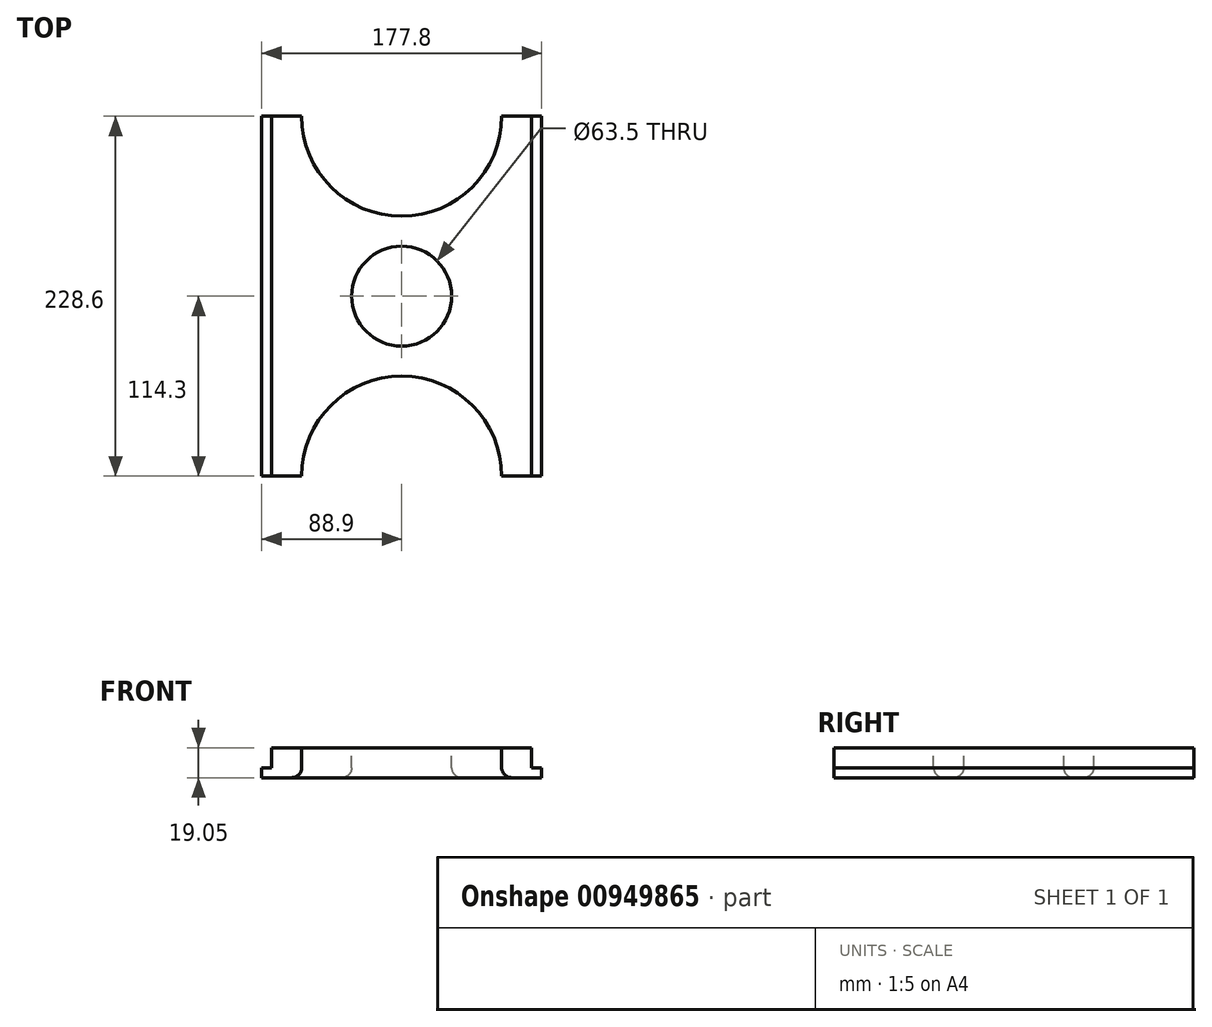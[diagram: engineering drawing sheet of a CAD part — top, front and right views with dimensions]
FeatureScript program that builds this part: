
annotation { "Feature Type Name" : "Feature", "Feature Type Description" : "" }
export const myFeature = defineFeature(function(context is Context, id is Id, definition is map)
    precondition{}
    {
        {
            var Q0;
            Q0=qCreatedBy(makeId("Top.planeOp"),FACE);
            var sketch = newSketch(context, id + "F0", { "sketchPlane" : qUnion([Q0])});
            skLineSegment(sketch, "E0.bottom", {"start": v(88.9, -114.3) * mm, "end": v(-88.9, -114.3) * mm});
            skLineSegment(sketch, "E0.top", {"start": v(88.9, 114.3) * mm, "end": v(-88.9, 114.3) * mm});
            skLineSegment(sketch, "E0.left", {"start": v(88.9, -114.3) * mm, "end": v(88.9, 114.3) * mm});
            skLineSegment(sketch, "E0.right", {"start": v(-88.9, -114.3) * mm, "end": v(-88.9, 114.3) * mm});
            skPoint(sketch, "E0.middle", {"position": v(0, 0) * mm});
            skSolve(sketch);
        }
        {
            var Q0;
            Q0 = qSketchRegion(id + "F0", true);
            extrude(context, id + "F1", {"entities" : qUnion([Q0]), "depth" : 19.05 * mm, "offsetDistance" : 25.4 * mm});
        }
        {
            var Q0;
            Q0=makeQuery(id+"F1.opExtrude","SWEPT_FACE",FACE,{"disambiguationData":[OSD([sQuery(id+"F0.wireOp",EDGE,"E0.bottom")])]});
            var sketch = newSketch(context, id + "F2", { "sketchPlane" : qUnion([Q0])});
            skLineSegment(sketch, "E1", {"start": v(82.55, 19.05) * mm, "end": v(82.55, 6.35) * mm});
            skLineSegment(sketch, "E2", {"start": v(82.55, 6.35) * mm, "end": v(88.9, 6.35) * mm});
            skLineSegment(sketch, "E3", {"start": v(88.9, 6.35) * mm, "end": v(88.9, 19.05) * mm});
            skLineSegment(sketch, "E4", {"start": v(88.9, 19.05) * mm, "end": v(82.55, 19.05) * mm});
            skLineSegment(sketch, "E5", {"start": v(-82.55, 19.05) * mm, "end": v(-82.55, 6.35) * mm});
            skLineSegment(sketch, "E6", {"start": v(-82.55, 6.35) * mm, "end": v(-88.9, 6.35) * mm});
            skLineSegment(sketch, "E7", {"start": v(-88.9, 6.35) * mm, "end": v(-88.9, 19.05) * mm});
            skLineSegment(sketch, "E8", {"start": v(-88.9, 19.05) * mm, "end": v(-82.55, 19.05) * mm});
            skSolve(sketch);
        }
        {
            var Q0;
            Q0 = qSketchRegion(id + "F2", true);
            extrude(context, id + "F3", {"entities" : qUnion([Q0]), "operationType" : NewBodyOperationType.REMOVE, "oppositeDirection" : true, "depth" : 254 * mm, "offsetDistance" : 25.4 * mm});
        }
        {
            var Q0;
            Q0=makeQuery(id+"F1.opExtrude","CAP_FACE",FACE,{"disambiguationData":[OSD([sQuery(id+"F0.wireOp",EDGE,"E0.bottom"),sQuery(id+"F0.wireOp",EDGE,"E0.top"),sQuery(id+"F0.wireOp",EDGE,"E0.left"),sQuery(id+"F0.wireOp",EDGE,"E0.right")])],"isStart":false});
            var sketch = newSketch(context, id + "F4", { "sketchPlane" : qUnion([Q0])});
            skLineSegment(sketch, "E9", {"start": v(0, 114.3) * mm, "end": v(0, -114.3) * mm, "construction": true});
            skLineSegment(sketch, "E10", {"start": v(-82.55, 0) * mm, "end": v(82.55, 0) * mm, "construction": true});
            skCircle(sketch, "E11", {"center": v(0, -114.3) * mm, "radius": 63.5 * mm});
            skCircle(sketch, "E12", {"center": v(0, 114.3) * mm, "radius": 63.5 * mm});
            skCircle(sketch, "E13", {"center": v(0, 0) * mm, "radius": 31.75 * mm});
            skSolve(sketch);
        }
        {
            var Q0;
            Q0 = qSketchRegion(id + "F4", true);
            extrude(context, id + "F5", {"entities" : qUnion([Q0]), "operationType" : NewBodyOperationType.REMOVE, "oppositeDirection" : true, "depth" : 25.4 * mm, "offsetDistance" : 25.4 * mm});
        }
        {
            var Q0;
            Q0=makeQuery(id+"F5.boolean.opBoolean","INTERSECT",EDGE,{"derivedFrom":[makeQuery(id+"F1.opExtrude","CAP_FACE",FACE,{"disambiguationData":[OSD([sQuery(id+"F0.wireOp",EDGE,"E0.bottom"),sQuery(id+"F0.wireOp",EDGE,"E0.top"),sQuery(id+"F0.wireOp",EDGE,"E0.left"),sQuery(id+"F0.wireOp",EDGE,"E0.right")])],"isStart":true}),makeQuery(id+"F5.opExtrude","SWEPT_FACE",FACE,{"disambiguationData":[OSD([sQuery(id+"F4.wireOp",EDGE,"E12")])]})]});
            var Q1;
            Q1=makeQuery(id+"F5.boolean.opBoolean","INTERSECT",EDGE,{"derivedFrom":[makeQuery(id+"F1.opExtrude","CAP_FACE",FACE,{"disambiguationData":[OSD([sQuery(id+"F0.wireOp",EDGE,"E0.bottom"),sQuery(id+"F0.wireOp",EDGE,"E0.top"),sQuery(id+"F0.wireOp",EDGE,"E0.left"),sQuery(id+"F0.wireOp",EDGE,"E0.right")])],"isStart":true}),makeQuery(id+"F5.opExtrude","SWEPT_FACE",FACE,{"disambiguationData":[OSD([sQuery(id+"F4.wireOp",EDGE,"E13")])]})]});
            var Q2;
            Q2=makeQuery(id+"F5.boolean.opBoolean","INTERSECT",EDGE,{"derivedFrom":[makeQuery(id+"F1.opExtrude","CAP_FACE",FACE,{"disambiguationData":[OSD([sQuery(id+"F0.wireOp",EDGE,"E0.bottom"),sQuery(id+"F0.wireOp",EDGE,"E0.top"),sQuery(id+"F0.wireOp",EDGE,"E0.left"),sQuery(id+"F0.wireOp",EDGE,"E0.right")])],"isStart":true}),makeQuery(id+"F5.opExtrude","SWEPT_FACE",FACE,{"disambiguationData":[OSD([sQuery(id+"F4.wireOp",EDGE,"E11")])]})]});
            var Q3;
            Q3=makeQuery(id+"F5.boolean.opBoolean","COPY",EDGE,{"derivedFrom":makeQuery(id+"F5.opExtrude","CAP_EDGE",EDGE,{"disambiguationData":[OSD([sQuery(id+"F4.wireOp",EDGE,"E12")])],"isStart":true})});
            var Q4;
            Q4=makeQuery(id+"F5.boolean.opBoolean","COPY",EDGE,{"derivedFrom":makeQuery(id+"F5.opExtrude","CAP_EDGE",EDGE,{"disambiguationData":[OSD([sQuery(id+"F4.wireOp",EDGE,"E13")])],"isStart":true})});
            var Q5;
            Q5=makeQuery(id+"F5.boolean.opBoolean","COPY",EDGE,{"derivedFrom":makeQuery(id+"F5.opExtrude","CAP_EDGE",EDGE,{"disambiguationData":[OSD([sQuery(id+"F4.wireOp",EDGE,"E11")])],"isStart":true})});
            fillet(context, id + "F6", {"entities" : qUnion([Q0, Q1, Q2, Q3, Q4, Q5]), "radius" : 6.35 * mm, "tangentPropagation" : true, "allowEdgeOverflow" : false});
        }
    });
